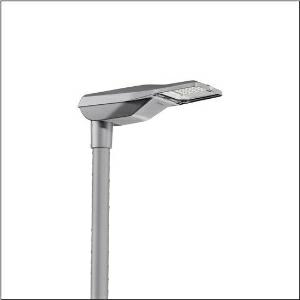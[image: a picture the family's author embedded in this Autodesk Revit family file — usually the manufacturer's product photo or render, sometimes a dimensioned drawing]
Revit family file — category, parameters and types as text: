
# Revit family: streetlight_sl_21_iq_micro___st1_5a_5xe1p41g08db_1f20
name_source: partatom
category: Lighting Fixtures
units: mm (PartAtom-declared; Revit-internal decimal feet)

## family parameters
Cut with Voids When Loaded = No
Host = Face
Light Source = No
Part Type = Normal
Room Calculation Point = No
Round Connector Dimension = Use Diameter
Shared = No

## types (1)
- --- (1 x LED, 4930 lm, 36.4 W, 4000K)
    Apparent Load = 36 VA
    CIE Flux Codes = 22 53 95 100 100
    Color Rendering = 70
    Color Temperature = 4000K
    Default Elevation = 1800 mm
    Description = Streetlight SL 21 iQ micro, mast luminaire, primary light control with lens, of PMMA, primary optical cover: cover, of toughened safety glass, transparent, light distribution: ST1.5a, light emission: direct distribution, primary light characteristic: asymmetric, installation type: post-top, side-entry, LED, High Power LED, rated luminous flux: 4.930lm, luminous efficacy: 135lm/W, light colour: 740, colour temperature: 4000K, control gear: iQ Street-Remote, control: Street-Remote, Auto-Match, Temp-Guard, Lumen-Switch, Night-Set, Smart-Wire, Light-Fading, Desk-Remote (wireless, voltage-free reading and setting of iQ features in the workshop via application-optimized NFC function/RFID function), optimised constant luminous flux control (CLO 2.0), pre-setting: linear dimming characteristic, mains connection: 220..240V, AC, 50/60Hz, start of lifetime: 36W, end of service life: 38W, reduction: 16W, luminaire housing, of diecast aluminium, powder-coated, Siteco® metallic grey (DB 702S), corrosivity category C5 mid according to DIN EN ISO 12944, please order mast flange separately, inclination adjustable: 0°, 5°, 10°, 15°, sealing non-destructively replaceable, multi-level sealing system, length: 528mm, width: 235mm, height: 110mm, mast flange for spigot size: 42mm (side-entry): 5XC10008XM4, 60/48mm (side-entry/post-top): 5XC10108XM2, 76/60mm (side-entry/post-top): 5XC10108XM1, protection rating (complete): IP66, insulation class (complete): insulation class II (safety insulation), certification: CE, ENEC, ENEC+, VDE, impact resistance: IK10, permissible operating ambient temperature for outdoor applications: -40..+50°C, standard-compliant lighting for roads and squares, packaging unit: 1 piece

Light Distribution: ST1.5a
    Height = 110 mm
    Lamp = 1 x LED
    Lamp Light Flux = 4930 lm
    Lamp Power = 36.4 W
    Lamp count = 1
    Length = 528 mm
    Luminous efficacy = 135 lm/W
    Manufacturer = Siteco
    ModVariant = No
    Model = 5XE1P41G08DB
    Number of Poles = 1
    OnlyDefault = Yes
    Power Factor = 1
    Product Name = Streetlight SL 21 iQ micro | ST1.5a
    Product group = mast luminaire | pylon top
    ProductGroupID = 6100
    Protection Class = Protection class II
    Protection Degree = IP 66
    RLX_Detail_Level = 1
    RLX_Emergency_Light_Flux = 0 lm
    RLX_Emergency_Type = 0
    RLX_Emergency_Type_DB = No
    RlxData = <blob elided: 103009 chars, md5=a2660920>
    Socket = socket
    Standby Power = 0 W
    System Light Flux = 4930 lm
    System Power = 36 W
    Type Comments = factory setting: luminous flux: 100 % | dim-lin: 254 | 715 mA
    Type Image = l_1006881.jpg
    URL = http://relux.com
    VarID = @adj_153826
    Voltage = 0 V
    Weight = 0.00 kg
    Width = 235 mm

## geometry (parser evidence)
native form markers: Blend x4, Sweep x11
no freeform markers — native parametric forms only
